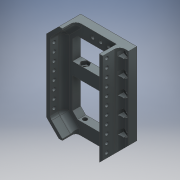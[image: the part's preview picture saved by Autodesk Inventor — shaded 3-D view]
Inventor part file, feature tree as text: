
AUTODESK INVENTOR PART (.ipt)
format: ipt  version: 2016 (Build 200138000, 138)  size: 484,352 bytes
history: native  units: mm
features: extrude x10, sketch x10, fillet x6, projected_geometry x2
ambient origin geometry x8: Origin, YZ Plane, XZ Plane, XY Plane, X Axis, Y Axis, Z Axis, Center Point
bodies: Body1 (feature_tree)
feature tree (28):
  extrude  "Extrusion2"  Depth=82.5mm
  extrude  "Extrusion7"  TaperAngle=135.0deg  [1 undecoded]
  extrude  "Extrusion8"  Depth=18.0mm
  extrude  "Extrusion9"  Depth=18.0mm
  extrude  "Extrusion11"  Depth=18.0mm
  extrude  "Extrusion12"  Depth=5.0mm
  fillet  "Fillet1"  Radius=5.0mm
  extrude  "Extrusion13"  Depth=5.0mm
  fillet  "Fillet2"  Radius=11.625mm
  fillet  "Fillet3"  Radius=9.0mm
  fillet  "Fillet4"  [1 undecoded]
  fillet  "Fillet5"  Radius=45.5mm
  fillet  "Fillet6"  Radius=45.5mm
  extrude  "Extrusion14"  Depth=18.0mm
  extrude  "Extrusion15"  Depth=18.0mm
  extrude  "Extrusion17"  TaperAngle=45.0deg  [1 undecoded]
  sketch  "Sketch1"  dims[d1=142.5mm d3=82.5mm]
  sketch  "Sketch7"  dims[d4=60.0mm d5=135.0deg]
  sketch  "Sketch8"  dims[d6=120.0mm d8=18.0mm]
  sketch  "Sketch9"  dims[d10=18.0mm d11=18.0mm d17=18.0mm]
  sketch  "Sketch11"  dims[d20=18.0mm d21=18.0mm]
  sketch  "Sketch12"  dims[d22=12.0mm d23=0.0mm d47=5.0mm d48=5.0mm]
  sketch  "Sketch13"  dims[d49=5.0mm d50=11.625mm d51=11.625mm d52=9.0mm d54=0.0mm d55=0.0mm d58=45.5mm d59=45.5mm]
  sketch  "Sketch14"  dims[d61=18.0mm d63=18.0mm]
  sketch  "Sketch15"  dims[d65=18.0mm d66=18.0mm]
  projected_geometry  "Projected Loop1"
  projected_geometry  "Projected Loop2"
  sketch  "Sketch17"  dims[d68=135.0deg d73=45.0deg d74=18.0mm d75=36.0mm d76=64.5mm d77=64.5mm d78=45.0deg d79=106.5mm d80=45.5mm d81=6.0mm d82=6.0mm d83=15.0mm d84=6.0mm d85=15.0mm d86=6.0mm d87=88.5mm d88=0.0mm d90=11.625mm d91=6.0mm d92=7.0mm d93=12.5mm d94=6.0mm d95=25.0mm d96=6.0mm d97=25.0mm d98=6.0mm d99=25.0mm d100=6.0mm d101=25.0mm d102=88.5mm d103=0.0mm d112=10.4mm d113=10.399866mm d114=10.4mm d118=10.4mm d119=10.4mm d120=5.0mm d121=0.0mm d122=5.0mm d123=5.0mm d124=4.5mm d125=25.0mm d126=0.0mm d127=8.0mm d131=5.0mm d132=5.0mm d133=5.0mm d134=5.0mm d135=5.0mm d136=20.0mm d137=0.0mm d138=8.0mm d139=8.0mm d140=8.0mm d141=5.25mm d142=8.0mm d143=5.0mm d144=6.0mm d145=6.0mm d146=5.0mm d147=5.0mm d148=12.0mm d149=12.0mm d150=12.0mm d151=12.0mm d152=5.0mm d153=0.0mm d154=5.0mm d156=6.0mm d157=5.0mm d158=12.0mm d159=12.0mm d160=12.0mm d163=142.5mm d164=5.0mm d165=0.0mm d170=10.4mm d171=10.4mm d172=5.0mm d173=0.0mm]
note: 3 required parameter values undecoded (feature->parameter linkage not recoverable at this tier; creation-order binding heuristic only, values carry confidence <= 0.55)
